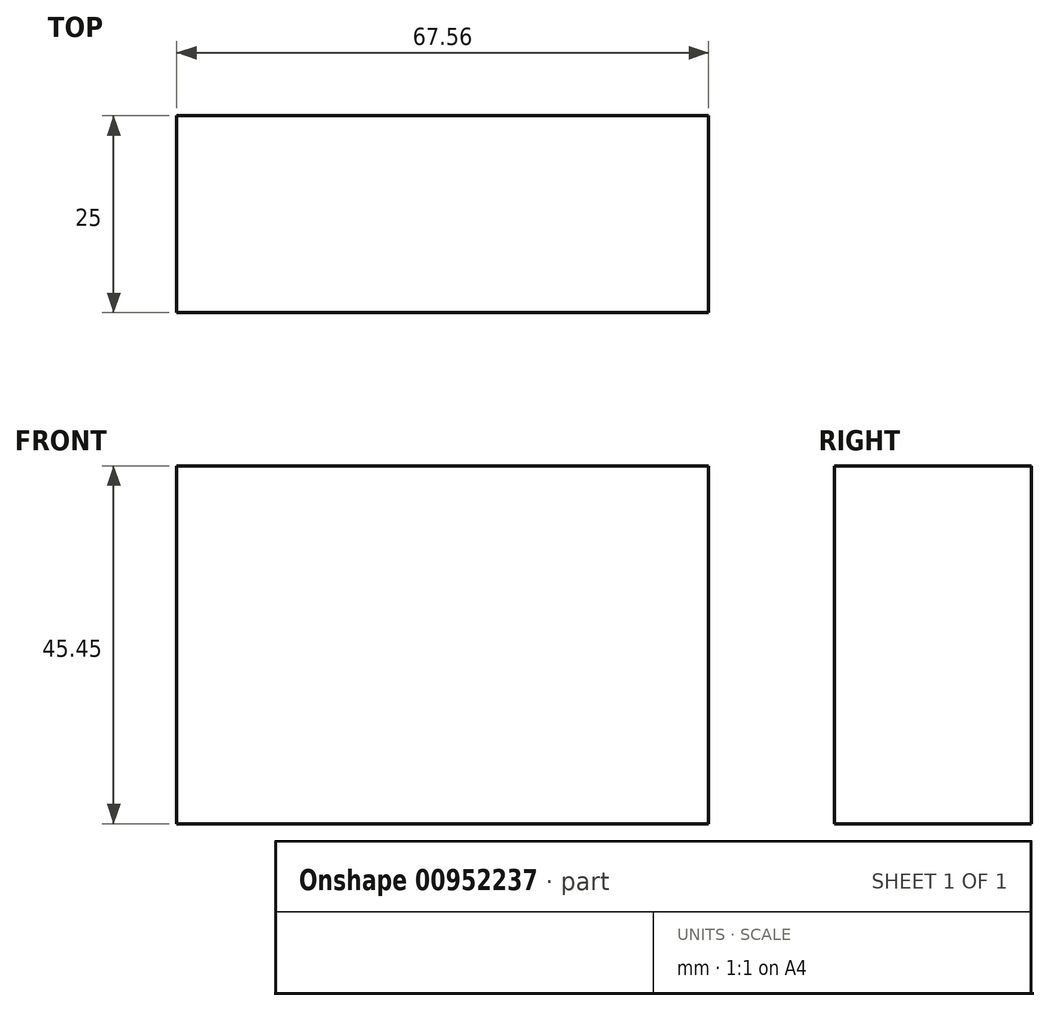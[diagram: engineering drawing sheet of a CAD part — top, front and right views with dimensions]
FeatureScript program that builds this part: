
annotation { "Feature Type Name" : "Feature", "Feature Type Description" : "" }
export const myFeature = defineFeature(function(context is Context, id is Id, definition is map)
    precondition{}
    {
        {
            var Q0;
            Q0=qCreatedBy(makeId("Front.planeOp"),FACE);
            var sketch = newSketch(context, id + "F0", { "sketchPlane" : qUnion([Q0])});
            skLineSegment(sketch, "E0.bottom", {"start": v(-29.24, 45.45) * mm, "end": v(38.32, 45.45) * mm});
            skLineSegment(sketch, "E0.top", {"start": v(-29.24, 0) * mm, "end": v(38.32, 0) * mm});
            skLineSegment(sketch, "E0.left", {"start": v(-29.24, 45.45) * mm, "end": v(-29.24, 0) * mm});
            skLineSegment(sketch, "E0.right", {"start": v(38.32, 45.45) * mm, "end": v(38.32, 0) * mm});
            skSolve(sketch);
        }
        {
            var Q0;
            Q0 = qSketchRegion(id + "F0", true);
            extrude(context, id + "F1", {"entities" : qUnion([Q0]), "depth" : 25 * mm, "offsetDistance" : 25 * mm});
        }
    });
